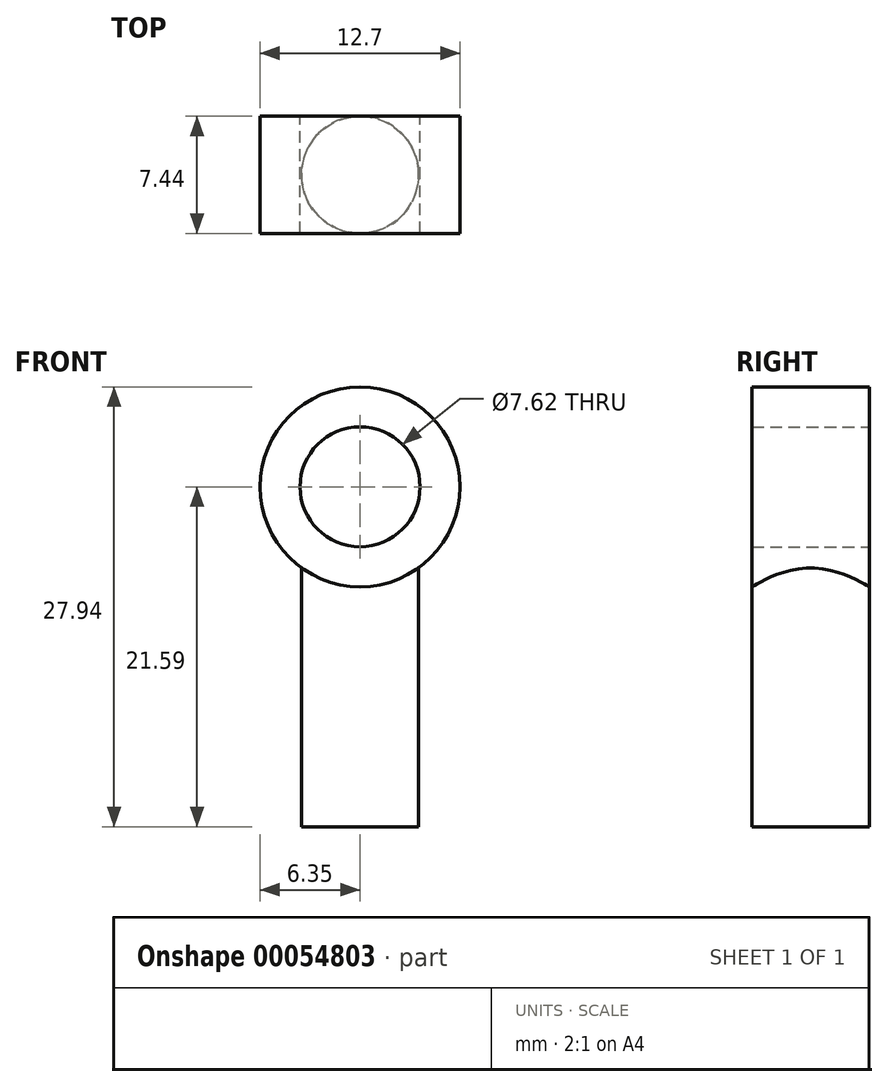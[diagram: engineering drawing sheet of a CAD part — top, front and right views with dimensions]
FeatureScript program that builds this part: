
annotation { "Feature Type Name" : "Feature", "Feature Type Description" : "" }
export const myFeature = defineFeature(function(context is Context, id is Id, definition is map)
    precondition{}
    {
        {
            var Q0;
            Q0=qCreatedBy(makeId("Top.planeOp"),FACE);
            var sketch = newSketch(context, id + "F0", { "sketchPlane" : qUnion([Q0])});
            skCircle(sketch, "E0", {"center": v(0, 0) * mm, "radius": 3.72 * mm});
            skSolve(sketch);
        }
        {
            var Q0;
            Q0 = qSketchRegion(id + "F0", true);
            extrude(context, id + "F1", {"entities" : qUnion([Q0]), "depth" : 15.24 * mm});
        }
        {
            var Q0;
            Q0=makeQuery(id+"F1.opExtrude","CAP_FACE",FACE,{"disambiguationData":[OSD([sQuery(id+"F0.wireOp",EDGE,"E0")])],"isStart":false});
            var sketch = newSketch(context, id + "F2", { "sketchPlane" : qUnion([Q0])});
            skSolve(sketch);
        }
        {
            var Q0;
            Q0=makeQuery(id+"F2.imprint","IMPRINT",FACE,{"disambiguationData":[TD([[makeQuery(id+"F2.imprint","IMPRINT",EDGE,{"derivedFrom":makeQuery(id+"F1.opExtrude","CAP_EDGE",EDGE,{"disambiguationData":[OSD([sQuery(id+"F0.wireOp",EDGE,"E0")])],"isStart":false})}),1.0]])]});
            var sketch = newSketch(context, id + "F3", { "sketchPlane" : qUnion([Q0])});
            skLineSegment(sketch, "E1.bottom", {"start": v(0, 0) * mm, "end": v(11.06, 0) * mm});
            skLineSegment(sketch, "E1.top", {"start": v(0, 5.09) * mm, "end": v(11.06, 5.09) * mm});
            skLineSegment(sketch, "E1.left", {"start": v(0, 0) * mm, "end": v(0, 5.09) * mm});
            skLineSegment(sketch, "E1.right", {"start": v(11.06, 0) * mm, "end": v(11.06, 5.09) * mm});
            skSolve(sketch);
        }
        {
            var Q0;
            Q0 = qSketchRegion(id + "F3", true);
            extrude(context, id + "F4", {"entities" : qUnion([Q0]), "operationType" : NewBodyOperationType.ADD, "depth" : 25.4 * mm});
        }
        {
            var Q0;
            Q0=makeQuery(id+"F4.opExtrude","SWEPT_FACE",FACE,{"disambiguationData":[OSD([sQuery(id+"F3.wireOp",EDGE,"E1.bottom")])]});
            var sketch = newSketch(context, id + "F5", { "sketchPlane" : qUnion([Q0])});
            skCircle(sketch, "E2", {"center": v(0, 21.59) * mm, "radius": 3.8 * mm});
            skCircle(sketch, "E3", {"center": v(0, 21.59) * mm, "radius": 6.35 * mm});
            skSolve(sketch);
        }
        {
            var Q0;
            Q0 = qSketchRegion(id + "F5", true);
            extrude(context, id + "F6", {"entities" : qUnion([Q0]), "depth" : 3.72 * mm});
        }
        {
            var Q0;
            Q0=makeQuery(id+"F4.opExtrude","CAP_FACE",FACE,{"disambiguationData":[OSD([sQuery(id+"F3.wireOp",EDGE,"E1.bottom"),sQuery(id+"F3.wireOp",EDGE,"E1.top"),sQuery(id+"F3.wireOp",EDGE,"E1.left"),sQuery(id+"F3.wireOp",EDGE,"E1.right")])],"isStart":false});
            var sketch = newSketch(context, id + "F7", { "sketchPlane" : qUnion([Q0])});
            skLineSegment(sketch, "E4.bottom", {"start": v(0, 5.09) * mm, "end": v(11.06, 5.09) * mm});
            skLineSegment(sketch, "E4.top", {"start": v(0, 0) * mm, "end": v(11.06, 0) * mm});
            skLineSegment(sketch, "E4.left", {"start": v(0, 5.09) * mm, "end": v(0, 0) * mm});
            skLineSegment(sketch, "E4.right", {"start": v(11.06, 5.09) * mm, "end": v(11.06, 0) * mm});
            skSolve(sketch);
        }
        {
            var Q0;
            Q0 = qSketchRegion(id + "F7", true);
            extrude(context, id + "F8", {"entities" : qUnion([Q0]), "operationType" : NewBodyOperationType.REMOVE, "oppositeDirection" : true, "depth" : 25.4 * mm});
        }
        {
            var Q0;
            Q0=makeQuery(id+"F6.opExtrude","CAP_FACE",FACE,{"disambiguationData":[OSD([sQuery(id+"F5.wireOp",EDGE,"E2"),sQuery(id+"F5.wireOp",EDGE,"E3")])],"isStart":true});
            var sketch = newSketch(context, id + "F9", { "sketchPlane" : qUnion([Q0])});
            skCircle(sketch, "E5", {"center": v(0, 21.59) * mm, "radius": 6.35 * mm});
            skCircle(sketch, "E6", {"center": v(0, 21.59) * mm, "radius": 3.81 * mm});
            skSolve(sketch);
        }
        {
            var Q0;
            Q0 = qSketchRegion(id + "F9", true);
            extrude(context, id + "F10", {"entities" : qUnion([Q0]), "depth" : 3.72 * mm});
        }
        {
            var Q0;
            Q0=makeQuery(id+"F2.imprint","IMPRINT",FACE,{"disambiguationData":[TD([[makeQuery(id+"F2.imprint","IMPRINT",EDGE,{"derivedFrom":makeQuery(id+"F1.opExtrude","CAP_EDGE",EDGE,{"disambiguationData":[OSD([sQuery(id+"F0.wireOp",EDGE,"E0")])],"isStart":false})}),1.0]])]});
            var sketch = newSketch(context, id + "F11", { "sketchPlane" : qUnion([Q0])});
            skCircle(sketch, "E7", {"center": v(0, 0) * mm, "radius": 3.72 * mm});
            skSolve(sketch);
        }
        {
            var Q0;
            Q0 = qSketchRegion(id + "F11", true);
            extrude(context, id + "F12", {"entities" : qUnion([Q0]), "operationType" : NewBodyOperationType.ADD, "depth" : 1.27 * mm});
        }
    });
